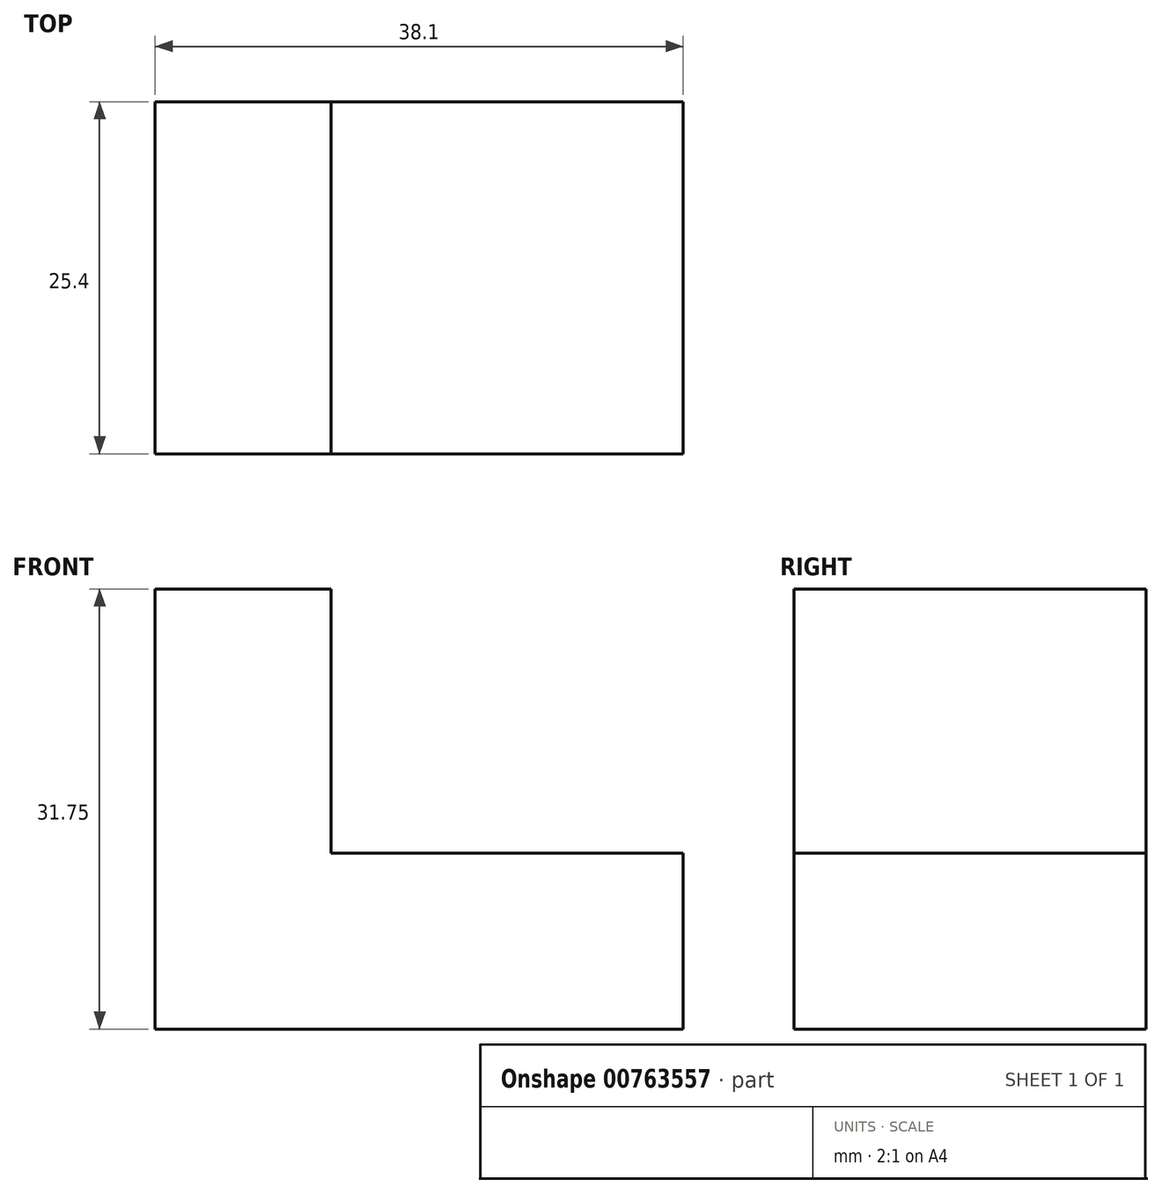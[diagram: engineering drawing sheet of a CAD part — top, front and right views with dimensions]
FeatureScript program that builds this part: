
annotation { "Feature Type Name" : "Feature", "Feature Type Description" : "" }
export const myFeature = defineFeature(function(context is Context, id is Id, definition is map)
    precondition{}
    {
        {
            var Q0;
            Q0=qCreatedBy(makeId("Front.planeOp"),FACE);
            var sketch = newSketch(context, id + "F0", { "sketchPlane" : qUnion([Q0])});
            skLineSegment(sketch, "E0", {"start": v(0, 0) * mm, "end": v(38.1, 0) * mm});
            skLineSegment(sketch, "E1", {"start": v(0, 0) * mm, "end": v(0, 31.75) * mm});
            skLineSegment(sketch, "E2", {"start": v(38.1, 0) * mm, "end": v(38.1, 12.7) * mm});
            skLineSegment(sketch, "E3", {"start": v(38.1, 12.7) * mm, "end": v(12.7, 12.7) * mm});
            skLineSegment(sketch, "E4", {"start": v(12.7, 12.7) * mm, "end": v(12.7, 31.75) * mm});
            skLineSegment(sketch, "E5", {"start": v(12.7, 31.75) * mm, "end": v(0, 31.75) * mm});
            skSolve(sketch);
        }
        {
            var Q0;
            Q0 = qSketchRegion(id + "F0", true);
            extrude(context, id + "F1", {"entities" : qUnion([Q0]), "depth" : 25.4 * mm, "offsetDistance" : 25.4 * mm});
        }
    });
